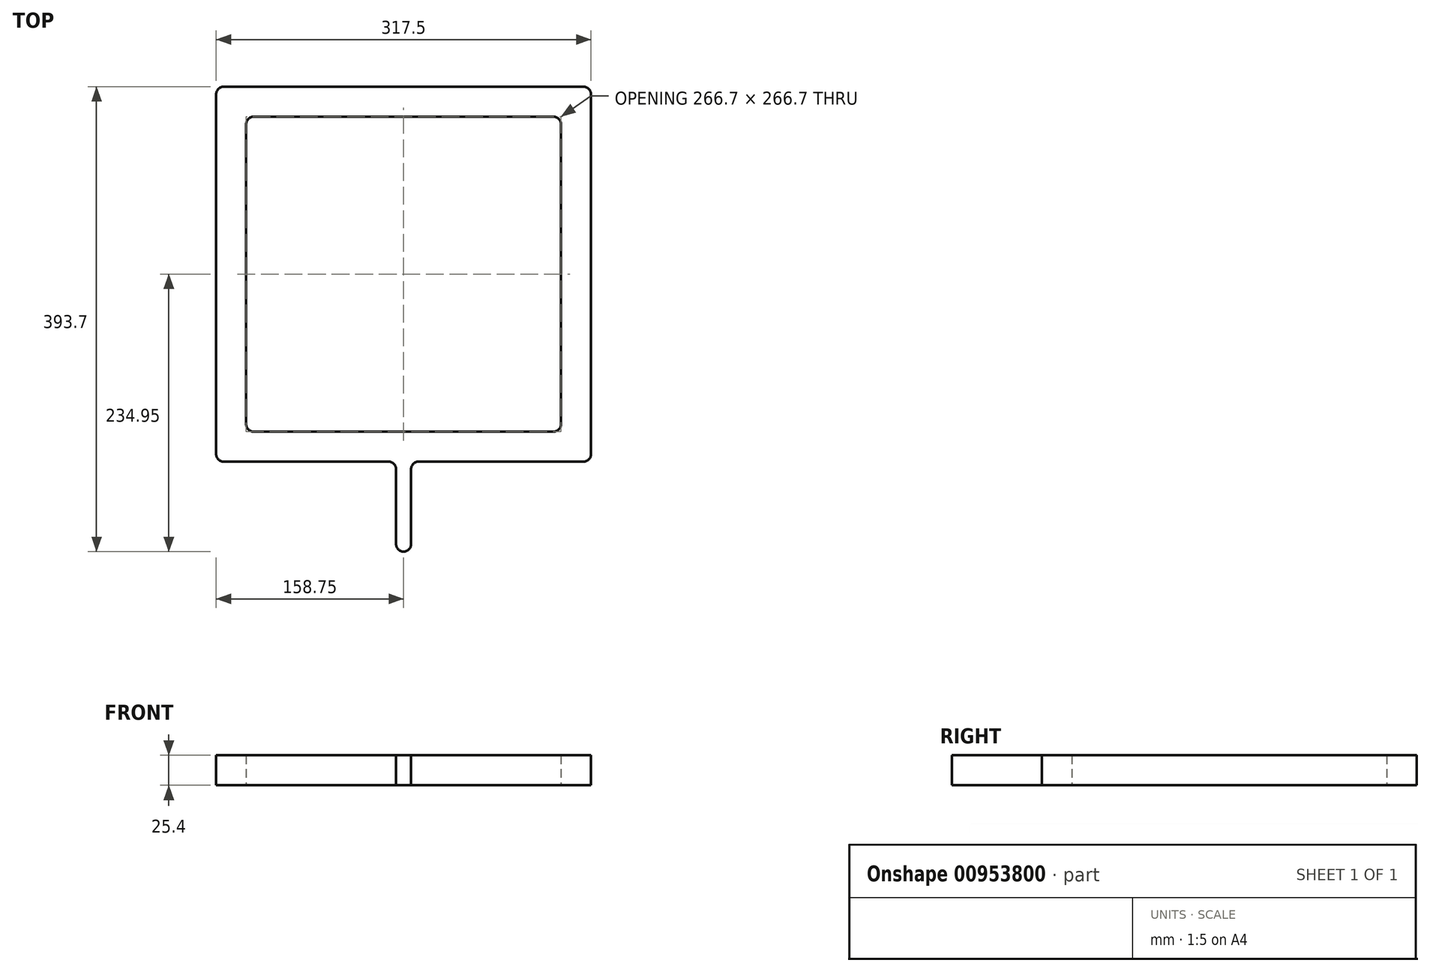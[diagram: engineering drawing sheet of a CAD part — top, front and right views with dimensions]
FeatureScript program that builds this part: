
annotation { "Feature Type Name" : "Feature", "Feature Type Description" : "" }
export const myFeature = defineFeature(function(context is Context, id is Id, definition is map)
    precondition{}
    {
        {
            var Q0;
            Q0=qCreatedBy(makeId("Top.planeOp"),FACE);
            var sketch = newSketch(context, id + "F0", { "sketchPlane" : qUnion([Q0])});
            skLineSegment(sketch, "E0.bottom", {"start": v(127, -133.35) * mm, "end": v(-127, -133.35) * mm});
            skLineSegment(sketch, "E0.top", {"start": v(127, 133.35) * mm, "end": v(-127, 133.35) * mm});
            skLineSegment(sketch, "E0.left", {"start": v(133.35, -127) * mm, "end": v(133.35, 127) * mm});
            skLineSegment(sketch, "E0.right", {"start": v(-133.35, -127) * mm, "end": v(-133.35, 127) * mm});
            skPoint(sketch, "E0.middle", {"position": v(0, 0) * mm});
            skLineSegment(sketch, "E1.bottom", {"start": v(152.4, -158.75) * mm, "end": v(12.7, -158.75) * mm});
            skLineSegment(sketch, "E1.top", {"start": v(152.4, 158.75) * mm, "end": v(-152.4, 158.75) * mm});
            skLineSegment(sketch, "E1.left", {"start": v(158.75, -152.4) * mm, "end": v(158.75, 152.4) * mm});
            skLineSegment(sketch, "E1.right", {"start": v(-158.75, -152.4) * mm, "end": v(-158.75, 152.4) * mm});
            skPoint(sketch, "E2.visualSharp", {"position": v(-158.75, 158.75) * mm});
            skArc(sketch, "E2.filletArc", {"start": v(-152.4, 158.75) * mm, "mid": v(-156.9, 156.9) * mm, "end": v(-158.75, 152.4) * mm});
            skPoint(sketch, "E3.visualSharp", {"position": v(158.75, 158.75) * mm});
            skArc(sketch, "E3.filletArc", {"start": v(158.75, 152.4) * mm, "mid": v(156.9, 156.9) * mm, "end": v(152.4, 158.75) * mm});
            skPoint(sketch, "E4.visualSharp", {"position": v(158.75, -158.75) * mm});
            skArc(sketch, "E4.filletArc", {"start": v(152.4, -158.75) * mm, "mid": v(156.9, -156.9) * mm, "end": v(158.75, -152.4) * mm});
            skPoint(sketch, "E5.visualSharp", {"position": v(-158.75, -158.75) * mm});
            skArc(sketch, "E5.filletArc", {"start": v(-158.75, -152.4) * mm, "mid": v(-156.9, -156.9) * mm, "end": v(-152.4, -158.75) * mm});
            skPoint(sketch, "E6.visualSharp", {"position": v(-133.35, -133.35) * mm});
            skArc(sketch, "E6.filletArc", {"start": v(-133.35, -127) * mm, "mid": v(-131.5, -131.5) * mm, "end": v(-127, -133.35) * mm});
            skPoint(sketch, "E7.visualSharp", {"position": v(-133.35, 133.35) * mm});
            skArc(sketch, "E7.filletArc", {"start": v(-127, 133.35) * mm, "mid": v(-131.5, 131.5) * mm, "end": v(-133.35, 127) * mm});
            skPoint(sketch, "E8.visualSharp", {"position": v(133.35, 133.35) * mm});
            skArc(sketch, "E8.filletArc", {"start": v(133.35, 127) * mm, "mid": v(131.5, 131.5) * mm, "end": v(127, 133.35) * mm});
            skPoint(sketch, "E9.visualSharp", {"position": v(133.35, -133.35) * mm});
            skArc(sketch, "E9.filletArc", {"start": v(127, -133.35) * mm, "mid": v(131.5, -131.5) * mm, "end": v(133.35, -127) * mm});
            skLineSegment(sketch, "E10.top", {"start": v(0, -234.95) * mm, "end": v(0, -234.95) * mm});
            skLineSegment(sketch, "E10.left", {"start": v(6.35, -165.1) * mm, "end": v(6.35, -228.6) * mm});
            skLineSegment(sketch, "E10.right", {"start": v(-6.35, -165.1) * mm, "end": v(-6.35, -228.6) * mm});
            skPoint(sketch, "E10.middle", {"position": v(0, -196.85) * mm});
            skLineSegment(sketch, "E11.trimOffspring", {"start": v(-12.7, -158.75) * mm, "end": v(-152.4, -158.75) * mm});
            skPoint(sketch, "E12.visualSharp", {"position": v(-6.35, -158.75) * mm});
            skArc(sketch, "E12.filletArc", {"start": v(-6.35, -165.1) * mm, "mid": v(-8.2, -160.6) * mm, "end": v(-12.7, -158.75) * mm});
            skPoint(sketch, "E13.visualSharp", {"position": v(6.35, -158.75) * mm});
            skArc(sketch, "E13.filletArc", {"start": v(12.7, -158.75) * mm, "mid": v(8.2, -160.6) * mm, "end": v(6.35, -165.1) * mm});
            skPoint(sketch, "E14.visualSharp", {"position": v(6.35, -234.95) * mm});
            skArc(sketch, "E14.filletArc", {"start": v(0, -234.95) * mm, "mid": v(4.5, -233.1) * mm, "end": v(6.35, -228.6) * mm});
            skPoint(sketch, "E15.visualSharp", {"position": v(-6.35, -234.95) * mm});
            skArc(sketch, "E15.filletArc", {"start": v(-6.35, -228.6) * mm, "mid": v(-4.5, -233.1) * mm, "end": v(0, -234.95) * mm});
            skSolve(sketch);
        }
        {
            var Q0;
            Q0=makeQuery(id+"F0.imprint","IMPRINT",FACE,{"disambiguationData":[TD([[makeQuery(id+"F0.imprint","IMPRINT",EDGE,{"derivedFrom":sQuery(id+"F0.wireOp",EDGE,"E0.bottom")}),1.0]])]});
            extrude(context, id + "F1", {"entities" : qUnion([Q0]), "depth" : 25.4 * mm, "offsetDistance" : 25.4 * mm});
        }
    });
